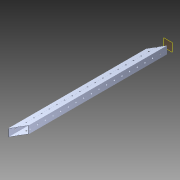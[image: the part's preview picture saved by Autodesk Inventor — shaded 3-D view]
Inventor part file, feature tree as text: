
AUTODESK INVENTOR PART (.ipt)
format: ipt  version: 2014 SP1 (Build 180222100, 222)  size: 1,287,168 bytes
history: native  units: in
note: dims shown in document units (in); Inventor stores cm internally (conversion verified against a paired STEP export)
features: extrude x3, sketch x3, pattern_circular x1, other x1, plane x1, imported_body x1
ambient origin geometry x8: Origin, YZ Plane, XZ Plane, XY Plane, X Axis, Y Axis, Z Axis, Center Point
bodies: Body1 (feature_tree)
feature tree (10):
  pattern_circular  "CirPattern2"
  other  "217-3426-STEP1"
  plane  "Work Plane1"
  extrude  "Extrusion1"  Depth=3937.0079in TaperAngle=0.0deg
  extrude  "Extrusion3"  Depth=3.937in TaperAngle=0.0deg
  extrude  "Extrusion4"  [1 undecoded]
  imported_body  "Base1"
  sketch  "Sketch1"  dims[d0=-21.0in d1=3937.0079in d2=0.0in]
  sketch  "Sketch4"  dims[d5=3.937in d6=0.0in d7=3.937in d8=0.0in]
  sketch  "Sketch5"
note: 1 required parameter value undecoded (feature->parameter linkage not recoverable at this tier; creation-order binding heuristic only, values carry confidence <= 0.55)
